# Revit family: Gewindebolzen
name_source: partatom
category: HLS-Bauteile
revit_build: Autodesk Revit 2017 (Build: 20190507_1515(x64)
units: mm (PartAtom-declared; Revit-internal decimal feet)

## family parameters
Arbeitsebenenbasiert = Ja
Beim Laden mit Abzugskörper schneiden = Nein
Bemaßung runder Anschluss = Durchmesser verwenden
Gemeinsam genutzt = Ja
Immer vertikal = Nein
Raumberechnungspunkt = Nein
Teiletyp = Normal

## types (6) — shared parameters
D = 7 mm  [stored 0.0229659 ft]
D0 = 4 mm  [stored 0.0131234 ft]
Fabrikat = MEFA
Firma = MEFA Befestigungs- und Montagesysteme GmbH
Gewinde = M8
Kurztext1 = Gewindebolzen
Material = Stahl
Mengeneinheit = St
Oberflaeche = galvanisch verzinkt
Vorgabe-Ansicht = 1219 mm
vpe = 100 St

## per-type parameters (varying)
| type | Artikelnummer | EAN | Gewicht | Gewicht pro Bauteil | Kurztext2 | Länge |
| Gewindebolzen M 8x13 | 0766151 | 4250928417404 | 0.00 kg | 0.00 kg | M8 x 13 mm gvz | 13 mm |
| Gewindebolzen M 8x25 | 0766259 | 4250928417411 | 0.01 kg | 0.01 kg | M8 x 25 mm gvz | 25 mm  [stored 0.082021 ft] |
| Gewindebolzen M 8x35 | 0766356 | 4250928417428 | 0.01 kg | 0.01 kg | M8 x 35 mm gvz | 35 mm  [stored 0.114829 ft] |
| Gewindebolzen M 8x45 | 0766453 | 4250928417435 | 0.01 kg | 0.01 kg | M8 x 45 mm gvz | 45 mm  [stored 0.147638 ft] |
| Gewindebolzen M 8x55 | 0766550 | 4250928417442 | 0.02 kg | 0.02 kg | M8 x 55 mm gvz | 55 mm  [stored 0.180446 ft] |
| Gewindebolzen M 8x65 | 0766658 | 4250928417459 | 0.02 kg | 0.02 kg | M8 x 65 mm gvz | 65 mm  [stored 0.213255 ft] |

note: [stored X ft] marks values corroborated as IEEE doubles in the binary element streams (Revit-internal decimal feet)
